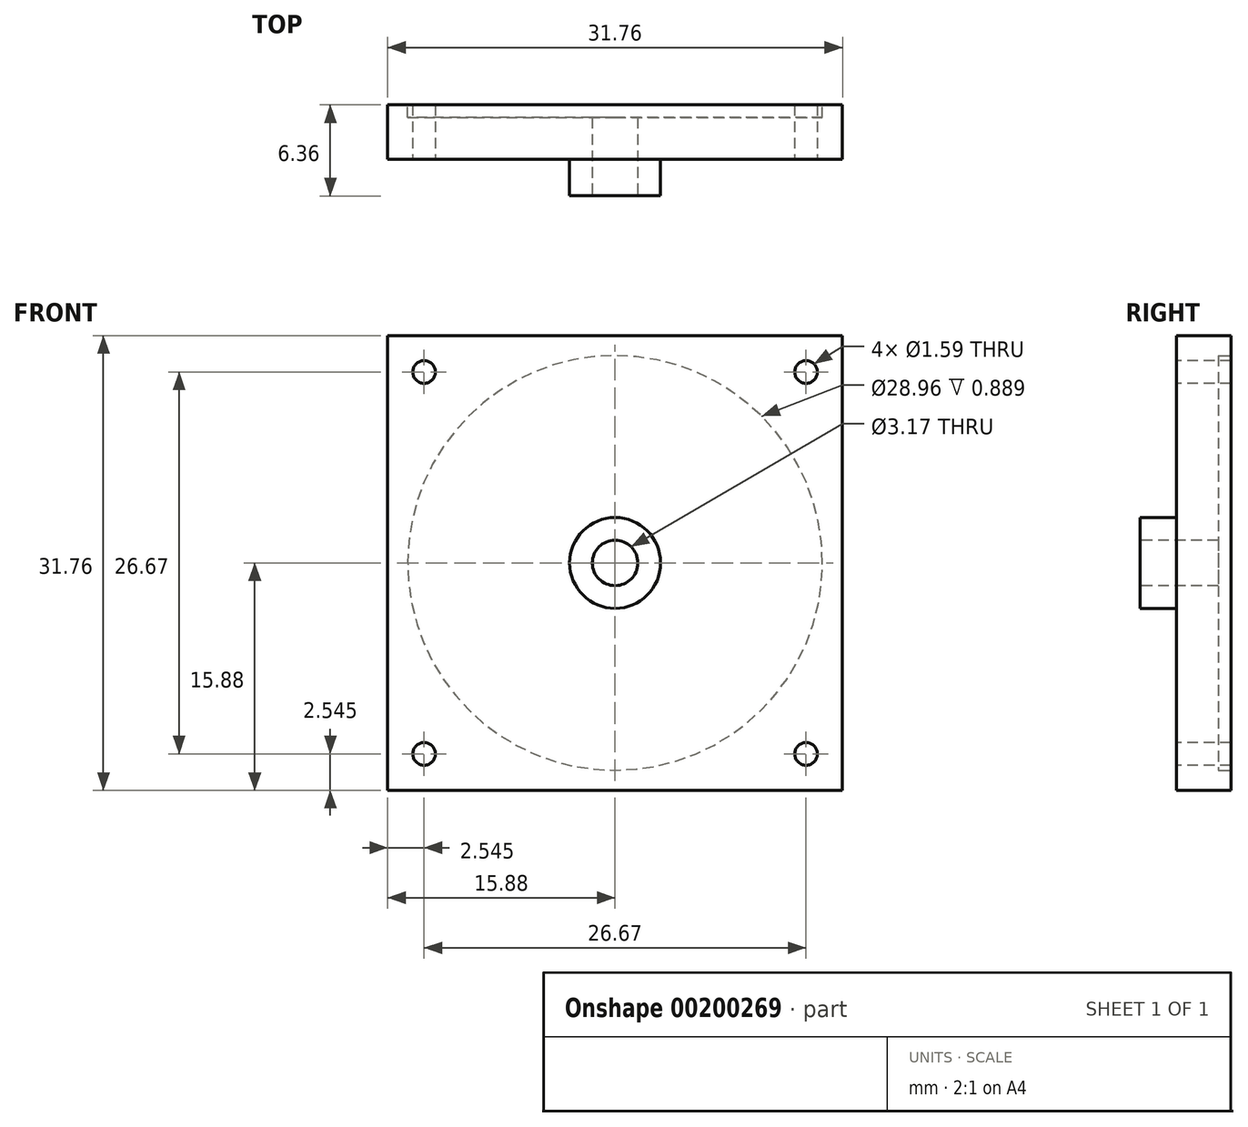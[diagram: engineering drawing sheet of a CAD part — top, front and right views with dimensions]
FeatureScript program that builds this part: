
annotation { "Feature Type Name" : "Feature", "Feature Type Description" : "" }
export const myFeature = defineFeature(function(context is Context, id is Id, definition is map)
    precondition{}
    {
        {
            var Q0;
            Q0=qCreatedBy(makeId("Front.planeOp"),FACE);
            var sketch = newSketch(context, id + "F0", { "sketchPlane" : qUnion([Q0])});
            skLineSegment(sketch, "E0.bottom", {"start": v(15.88, -15.88) * mm, "end": v(-15.88, -15.88) * mm});
            skLineSegment(sketch, "E0.top", {"start": v(15.88, 15.88) * mm, "end": v(-15.88, 15.87) * mm});
            skLineSegment(sketch, "E0.left", {"start": v(15.88, -15.88) * mm, "end": v(15.88, 15.88) * mm});
            skLineSegment(sketch, "E0.right", {"start": v(-15.88, -15.88) * mm, "end": v(-15.88, 15.87) * mm});
            skPoint(sketch, "E0.middle", {"position": v(0, 0) * mm});
            skSolve(sketch);
        }
        {
            var Q0;
            Q0=makeQuery(id+"F0.imprint","IMPRINT",FACE,{"disambiguationData":[TD([[makeQuery(id+"F0.imprint","IMPRINT",EDGE,{"derivedFrom":sQuery(id+"F0.wireOp",EDGE,"E0.bottom")}),-1.0]])]});
            extrude(context, id + "F1", {"entities" : qUnion([Q0]), "endBound" : BoundingType.SYMMETRIC, "offsetDistance" : 25.4 * mm, "depth" : 3.8 * mm});
        }
        {
            var Q0;
            Q0=makeQuery(id+"F1.opExtrude","CAP_FACE",FACE,{"disambiguationData":[OSD([sQuery(id+"F0.wireOp",EDGE,"E0.bottom"),sQuery(id+"F0.wireOp",EDGE,"E0.top"),sQuery(id+"F0.wireOp",EDGE,"E0.left"),sQuery(id+"F0.wireOp",EDGE,"E0.right")])],"isStart":true});
            var sketch = newSketch(context, id + "F2", { "sketchPlane" : qUnion([Q0])});
            skCircle(sketch, "E1", {"center": v(0, 0) * mm, "radius": 14.48 * mm});
            skSolve(sketch);
        }
        {
            var Q0;
            Q0=makeQuery(id+"F2.imprint","IMPRINT",FACE,{"disambiguationData":[TD([[makeQuery(id+"F2.imprint","IMPRINT",EDGE,{"derivedFrom":sQuery(id+"F2.wireOp",EDGE,"E1")}),1.0]])]});
            extrude(context, id + "F3", {"entities" : qUnion([Q0]), "operationType" : NewBodyOperationType.REMOVE, "oppositeDirection" : true, "depth" : 0.89 * mm});
        }
        {
            var Q0;
            Q0=makeQuery(id+"F1.opExtrude","CAP_FACE",FACE,{"disambiguationData":[OSD([sQuery(id+"F0.wireOp",EDGE,"E0.bottom"),sQuery(id+"F0.wireOp",EDGE,"E0.top"),sQuery(id+"F0.wireOp",EDGE,"E0.left"),sQuery(id+"F0.wireOp",EDGE,"E0.right")])],"isStart":false});
            var sketch = newSketch(context, id + "F4", { "sketchPlane" : qUnion([Q0])});
            skLineSegment(sketch, "E2.bottom", {"start": v(13.33, -13.33) * mm, "end": v(-13.34, -13.34) * mm});
            skLineSegment(sketch, "E2.top", {"start": v(13.34, 13.34) * mm, "end": v(-13.34, 13.33) * mm});
            skLineSegment(sketch, "E2.left", {"start": v(13.33, -13.33) * mm, "end": v(13.34, 13.33) * mm});
            skLineSegment(sketch, "E2.right", {"start": v(-13.34, -13.34) * mm, "end": v(-13.34, 13.33) * mm});
            skPoint(sketch, "E2.middle", {"position": v(0, 0) * mm});
            skSolve(sketch);
        }
        {
            var Q0;
            Q0=sQuery(id+"F4.wireOp",VERTEX,"E2.top.end");
            var Q1;
            Q1=sQuery(id+"F4.wireOp",VERTEX,"E2.left.end");
            var Q2;
            Q2=sQuery(id+"F4.wireOp",VERTEX,"E2.left.start");
            var Q3;
            Q3=sQuery(id+"F4.wireOp",VERTEX,"E2.right.start");
            var Q4;
            Q4=makeQuery(id+"F1.opExtrude","SWEPT_BODY",BODY,{"disambiguationData":[OSD([sQuery(id+"F0.wireOp",EDGE,"E0.bottom"),sQuery(id+"F0.wireOp",EDGE,"E0.top"),sQuery(id+"F0.wireOp",EDGE,"E0.left"),sQuery(id+"F0.wireOp",EDGE,"E0.right")])]});
            hole(context, id + "F5", {"style" : HoleStyle.SIMPLE, "endStyle" : HoleEndStyle.THROUGH, "holeDiameter" : 1.59 * mm, "locations" : qUnion([Q0, Q1, Q2, Q3]), "scope" : qUnion([Q4]), "isTappedThrough" : true});
        }
        {
            var Q0;
            Q0=makeQuery(id+"F1.opExtrude","CAP_FACE",FACE,{"disambiguationData":[OSD([sQuery(id+"F0.wireOp",EDGE,"E0.bottom"),sQuery(id+"F0.wireOp",EDGE,"E0.top"),sQuery(id+"F0.wireOp",EDGE,"E0.left"),sQuery(id+"F0.wireOp",EDGE,"E0.right")])],"isStart":false});
            var sketch = newSketch(context, id + "F6", { "sketchPlane" : qUnion([Q0])});
            skCircle(sketch, "E3", {"center": v(0, 0) * mm, "radius": 1.59 * mm});
            skCircle(sketch, "E4", {"center": v(0, 0) * mm, "radius": 6.35 * mm});
            skSolve(sketch);
        }
        {
            var Q0;
            Q0=makeQuery(id+"F6.imprint","IMPRINT",FACE,{"disambiguationData":[TD([[makeQuery(id+"F6.imprint","IMPRINT",EDGE,{"derivedFrom":sQuery(id+"F6.wireOp",EDGE,"E3")}),1.0]])]});
            extrude(context, id + "F7", {"entities" : qUnion([Q0]), "operationType" : NewBodyOperationType.REMOVE, "endBound" : BoundingType.THROUGH_ALL, "oppositeDirection" : true, "depth" : 25.4 * mm});
        }
        {
            var Q0;
            Q0=makeQuery(id+"F1.opExtrude","CAP_FACE",FACE,{"disambiguationData":[OSD([sQuery(id+"F0.wireOp",EDGE,"E0.bottom"),sQuery(id+"F0.wireOp",EDGE,"E0.top"),sQuery(id+"F0.wireOp",EDGE,"E0.left"),sQuery(id+"F0.wireOp",EDGE,"E0.right")])],"isStart":false});
            var sketch = newSketch(context, id + "F8", { "sketchPlane" : qUnion([Q0])});
            skCircle(sketch, "E5", {"center": v(0, 0) * mm, "radius": 3.18 * mm});
            skSolve(sketch);
        }
        {
            var Q0;
            Q0=makeQuery(id+"F8.imprint","IMPRINT",FACE,{"disambiguationData":[TD([[makeQuery(id+"F8.imprint","IMPRINT",EDGE,{"derivedFrom":sQuery(id+"F8.wireOp",EDGE,"E5")}),1.0]])]});
            extrude(context, id + "F9", {"entities" : qUnion([Q0]), "operationType" : NewBodyOperationType.ADD, "depth" : 2.54 * mm});
        }
    });
